# Revit family: Childrens coat rack N100 600
name_source: partatom
category: Casework
revit_build: Autodesk Revit MEP 2013 (Build: 20120221_2030(x64)
units: mm (PartAtom-declared; Revit-internal decimal feet)

## types (1)
- Childrens coat rack N100 600
    BIMobject Category = Furniture
    BIMobject QR code url = http://vaneritarvike.bimobject.com
    Back Panel Material = Valkoinen
    Bars And Bottom Panel Material = F0231
    Date of publishing = 4/2/2013
    Depth = 430 mm
    Design country = Finland
    Door Material = F4168
    Edition number = 2
    Height = 1520 mm
    IFC Classification = Furniture
    Legs Material = Musta
    Manufacture country = Finland
    Manufacturer = Nokian Vaneritarvike Oy
    Manufacturer URL = http://www.vaneritarvike.fi
    Middle Panels Material = koivu
    Middle Vertical Panel Material = koivu
    Model = Childrens coat rack N100 600
    Name of the object = Childrens coat rack N100 600
    Product SKU = 7500
    Product data url = http://www.vaneritarvike.fi
    Product family = Kindergarten Furniture
    Product group = Coat rack
    Rack Top and Bottom Panels Material = koivu
    Side Panels Material = koivu
    Support Panels Material = koivu
    UNSPC Category = Furniture and Furnishings
    UNSPC code = 56
    URL = http://vaneritarvike.bimobject.com
    Weight Net (kg) = 0 mm  [stored 0 ft]
    Width = 600 mm

note: [stored X ft] marks values corroborated as IEEE doubles in the binary element streams (Revit-internal decimal feet)

## geometry (parser evidence)
native form markers: Blend x118, Sweep x1
no freeform markers — native parametric forms only
